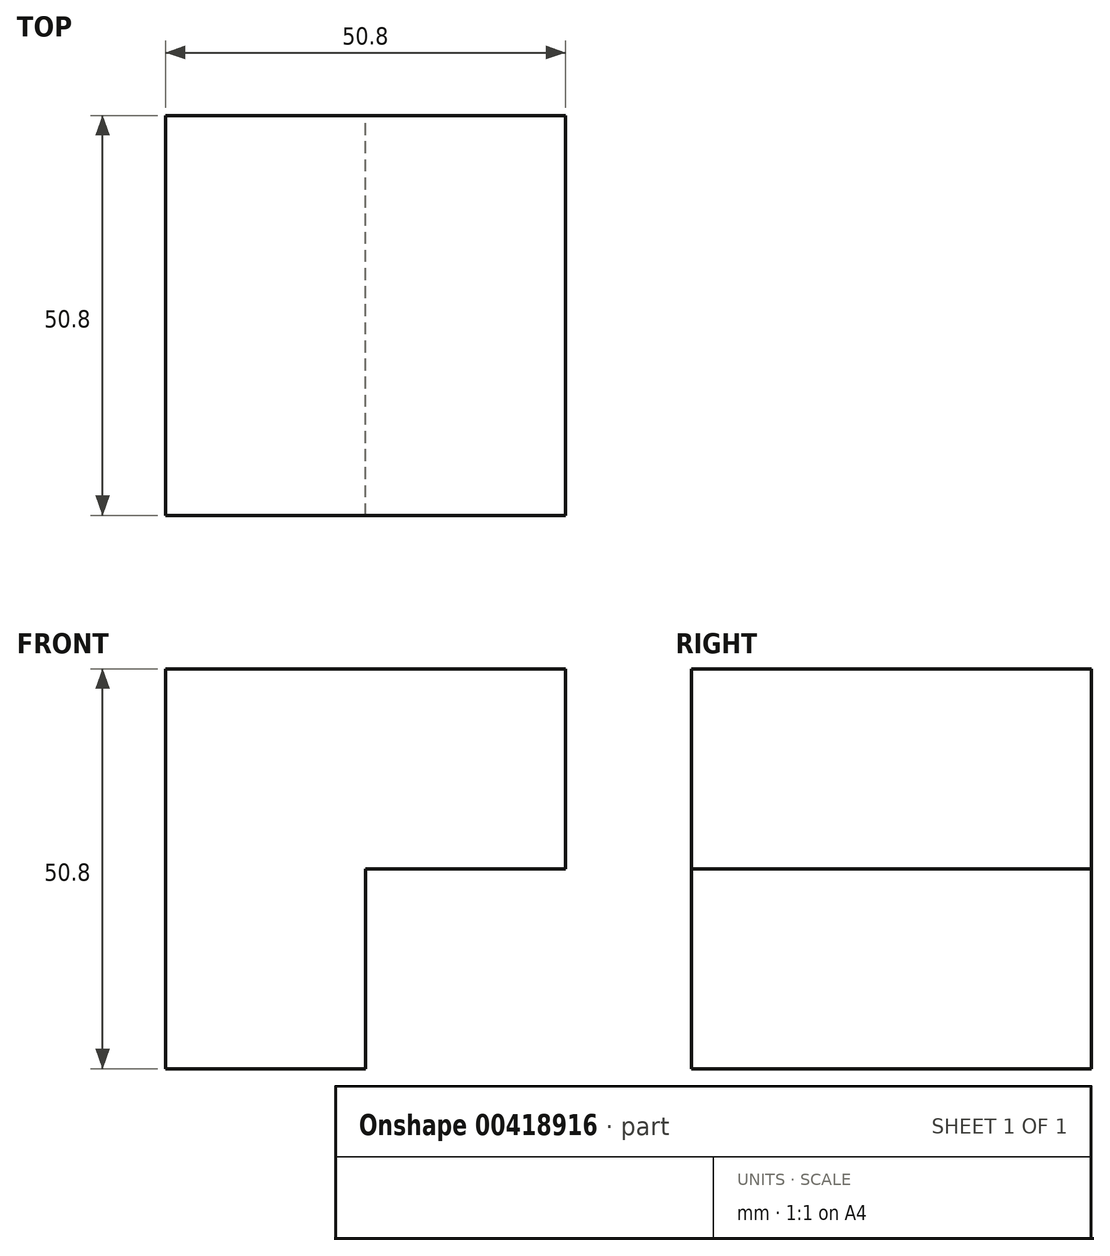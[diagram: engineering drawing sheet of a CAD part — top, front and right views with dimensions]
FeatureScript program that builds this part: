
annotation { "Feature Type Name" : "Feature", "Feature Type Description" : "" }
export const myFeature = defineFeature(function(context is Context, id is Id, definition is map)
    precondition{}
    {
        {
            var Q0;
            Q0=qCreatedBy(makeId("Front.planeOp"),FACE);
            var sketch = newSketch(context, id + "F0", { "sketchPlane" : qUnion([Q0])});
            skLineSegment(sketch, "E0", {"start": v(0, 0) * mm, "end": v(0, -25.4) * mm});
            skLineSegment(sketch, "E1", {"start": v(0, -25.4) * mm, "end": v(-25.4, -25.4) * mm});
            skLineSegment(sketch, "E2", {"start": v(-25.4, -25.4) * mm, "end": v(-25.4, -50.8) * mm});
            skLineSegment(sketch, "E3", {"start": v(-25.4, -50.8) * mm, "end": v(-50.8, -50.8) * mm});
            skLineSegment(sketch, "E4", {"start": v(-50.8, -50.8) * mm, "end": v(-50.8, 0) * mm});
            skLineSegment(sketch, "E5", {"start": v(-50.8, 0) * mm, "end": v(0, 0) * mm});
            skSolve(sketch);
        }
        {
            var Q0;
            Q0=makeQuery(id+"F0.imprint","IMPRINT",FACE,{"disambiguationData":[TD([[makeQuery(id+"F0.imprint","IMPRINT",EDGE,{"derivedFrom":sQuery(id+"F0.wireOp",EDGE,"E0")}),-1.0]])]});
            extrude(context, id + "F1", {"entities" : qUnion([Q0]), "depth" : 50.8 * mm});
        }
    });
